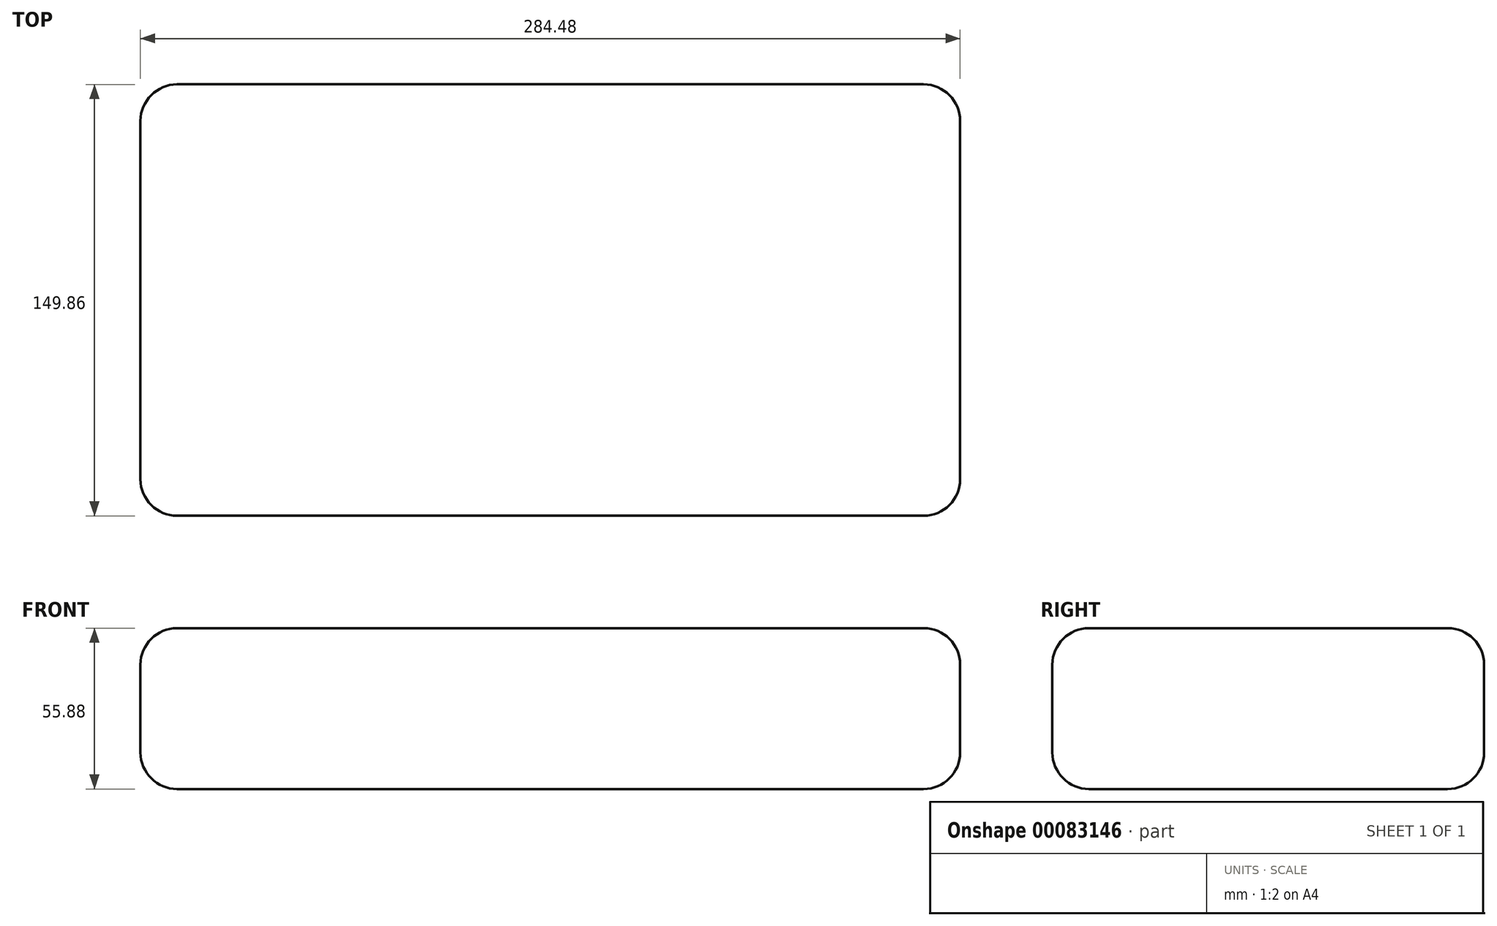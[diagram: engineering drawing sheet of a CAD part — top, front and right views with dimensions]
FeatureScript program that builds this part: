
annotation { "Feature Type Name" : "Feature", "Feature Type Description" : "" }
export const myFeature = defineFeature(function(context is Context, id is Id, definition is map)
    precondition{}
    {
        {
            var Q0;
            Q0=qCreatedBy(makeId("Top.planeOp"),FACE);
            var sketch = newSketch(context, id + "F0", { "sketchPlane" : qUnion([Q0])});
            skLineSegment(sketch, "E0.bottom", {"start": v(-325.5, 54.74) * mm, "end": v(-66.42, 54.74) * mm});
            skLineSegment(sketch, "E0.top", {"start": v(-325.5, -95.12) * mm, "end": v(-66.42, -95.12) * mm});
            skLineSegment(sketch, "E0.left", {"start": v(-338.2, 42.04) * mm, "end": v(-338.2, -82.42) * mm});
            skLineSegment(sketch, "E0.right", {"start": v(-53.72, 42.04) * mm, "end": v(-53.72, -82.42) * mm});
            skPoint(sketch, "E1.visualSharp", {"position": v(-53.72, 54.74) * mm});
            skArc(sketch, "E1.filletArc", {"start": v(-53.72, 42.04) * mm, "mid": v(-57.44, 51.02) * mm, "end": v(-66.42, 54.74) * mm});
            skPoint(sketch, "E2.visualSharp", {"position": v(-53.72, -95.12) * mm});
            skArc(sketch, "E2.filletArc", {"start": v(-66.42, -95.12) * mm, "mid": v(-57.44, -91.4) * mm, "end": v(-53.72, -82.42) * mm});
            skPoint(sketch, "E3.visualSharp", {"position": v(-338.2, -95.12) * mm});
            skArc(sketch, "E3.filletArc", {"start": v(-338.2, -82.42) * mm, "mid": v(-334.48, -91.4) * mm, "end": v(-325.5, -95.12) * mm});
            skPoint(sketch, "E4.visualSharp", {"position": v(-338.2, 54.74) * mm});
            skArc(sketch, "E4.filletArc", {"start": v(-325.5, 54.74) * mm, "mid": v(-334.48, 51.02) * mm, "end": v(-338.2, 42.04) * mm});
            skSolve(sketch);
        }
        {
            var Q0;
            Q0=makeQuery(id+"F0.imprint","IMPRINT",FACE,{"disambiguationData":[TD([[makeQuery(id+"F0.imprint","IMPRINT",EDGE,{"derivedFrom":sQuery(id+"F0.wireOp",EDGE,"E0.bottom")}),-1.0]])]});
            extrude(context, id + "F1", {"entities" : qUnion([Q0]), "depth" : 55.88 * mm});
        }
        {
            var Q0;
            Q0=makeQuery(id+"F1.opExtrude","CAP_FACE",FACE,{"disambiguationData":[OSD([sQuery(id+"F0.wireOp",EDGE,"E0.bottom"),sQuery(id+"F0.wireOp",EDGE,"E0.top"),sQuery(id+"F0.wireOp",EDGE,"E0.left"),sQuery(id+"F0.wireOp",EDGE,"E0.right"),sQuery(id+"F0.wireOp",EDGE,"E1.filletArc"),sQuery(id+"F0.wireOp",EDGE,"E2.filletArc"),sQuery(id+"F0.wireOp",EDGE,"E3.filletArc"),sQuery(id+"F0.wireOp",EDGE,"E4.filletArc")])],"isStart":false});
            var Q1;
            Q1=makeQuery(id+"F1.opExtrude","SWEPT_FACE",FACE,{"disambiguationData":[OSD([sQuery(id+"F0.wireOp",EDGE,"E0.top")])]});
            var Q2;
            Q2=makeQuery(id+"F1.opExtrude","SWEPT_FACE",FACE,{"disambiguationData":[OSD([sQuery(id+"F0.wireOp",EDGE,"E2.filletArc")])]});
            var Q3;
            Q3=makeQuery(id+"F1.opExtrude","SWEPT_FACE",FACE,{"disambiguationData":[OSD([sQuery(id+"F0.wireOp",EDGE,"E0.right")])]});
            var Q4;
            Q4=makeQuery(id+"F1.opExtrude","SWEPT_FACE",FACE,{"disambiguationData":[OSD([sQuery(id+"F0.wireOp",EDGE,"E1.filletArc")])]});
            var Q5;
            Q5=makeQuery(id+"F1.opExtrude","CAP_FACE",FACE,{"disambiguationData":[OSD([sQuery(id+"F0.wireOp",EDGE,"E0.bottom"),sQuery(id+"F0.wireOp",EDGE,"E0.top"),sQuery(id+"F0.wireOp",EDGE,"E0.left"),sQuery(id+"F0.wireOp",EDGE,"E0.right"),sQuery(id+"F0.wireOp",EDGE,"E1.filletArc"),sQuery(id+"F0.wireOp",EDGE,"E2.filletArc"),sQuery(id+"F0.wireOp",EDGE,"E3.filletArc"),sQuery(id+"F0.wireOp",EDGE,"E4.filletArc")])],"isStart":true});
            fillet(context, id + "F2", {"entities" : qUnion([Q0, Q1, Q2, Q3, Q4, Q5]), "radius" : 12.7 * mm, "tangentPropagation" : true, "allowEdgeOverflow" : false});
        }
    });
